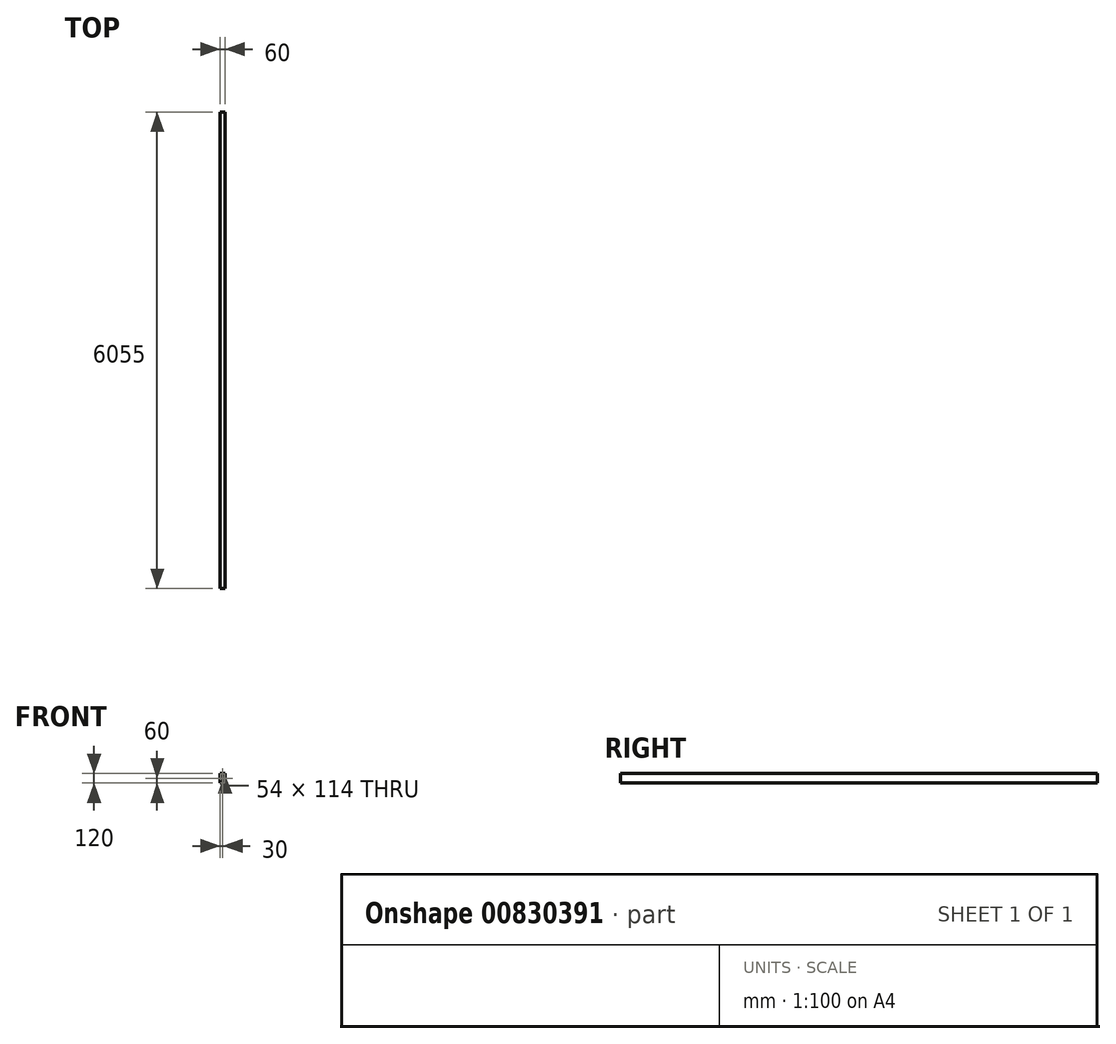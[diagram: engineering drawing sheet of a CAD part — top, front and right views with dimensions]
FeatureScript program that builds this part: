
annotation { "Feature Type Name" : "Feature", "Feature Type Description" : "" }
export const myFeature = defineFeature(function(context is Context, id is Id, definition is map)
    precondition{}
    {
        {
            var Q0;
            Q0=qCreatedBy(makeId("Front.planeOp"),FACE);
            var sketch = newSketch(context, id + "F0", { "sketchPlane" : qUnion([Q0])});
            skLineSegment(sketch, "E0.bottom", {"start": v(30, 60) * mm, "end": v(-30, 60) * mm});
            skLineSegment(sketch, "E0.top", {"start": v(30, -60) * mm, "end": v(-30, -60) * mm});
            skLineSegment(sketch, "E0.left", {"start": v(30, 60) * mm, "end": v(30, -60) * mm});
            skLineSegment(sketch, "E0.right", {"start": v(-30, 60) * mm, "end": v(-30, -60) * mm});
            skPoint(sketch, "E0.middle", {"position": v(0, 0) * mm});
            skLineSegment(sketch, "E1.0", {"start": v(-27, 57) * mm, "end": v(-27, -57) * mm});
            skLineSegment(sketch, "E1.1", {"start": v(27, 57) * mm, "end": v(-27, 57) * mm});
            skLineSegment(sketch, "E1.2", {"start": v(27, 57) * mm, "end": v(27, -57) * mm});
            skLineSegment(sketch, "E1.3", {"start": v(27, -57) * mm, "end": v(-27, -57) * mm});
            skSolve(sketch);
        }
        {
            var Q0;
            Q0=qCreatedBy(makeId("Right.planeOp"),FACE);
            var sketch = newSketch(context, id + "F1", { "sketchPlane" : qUnion([Q0])});
            skLineSegment(sketch, "E2", {"start": v(0, 0) * mm, "end": v(-6055, 0) * mm});
            skSolve(sketch);
        }
        {
            var Q0;
            Q0=qSketchRegion(id+"F0",true);
            var Q1;
            Q1=qConstructionFilter(qBodyType(qCreatedBy(id+"F1",EDGE),BodyType.WIRE),ConstructionObject.NO);
            sweep(context, id + "F2", {"profiles" : qUnion([Q0]), "path" : qUnion([Q1])});
        }
    });
